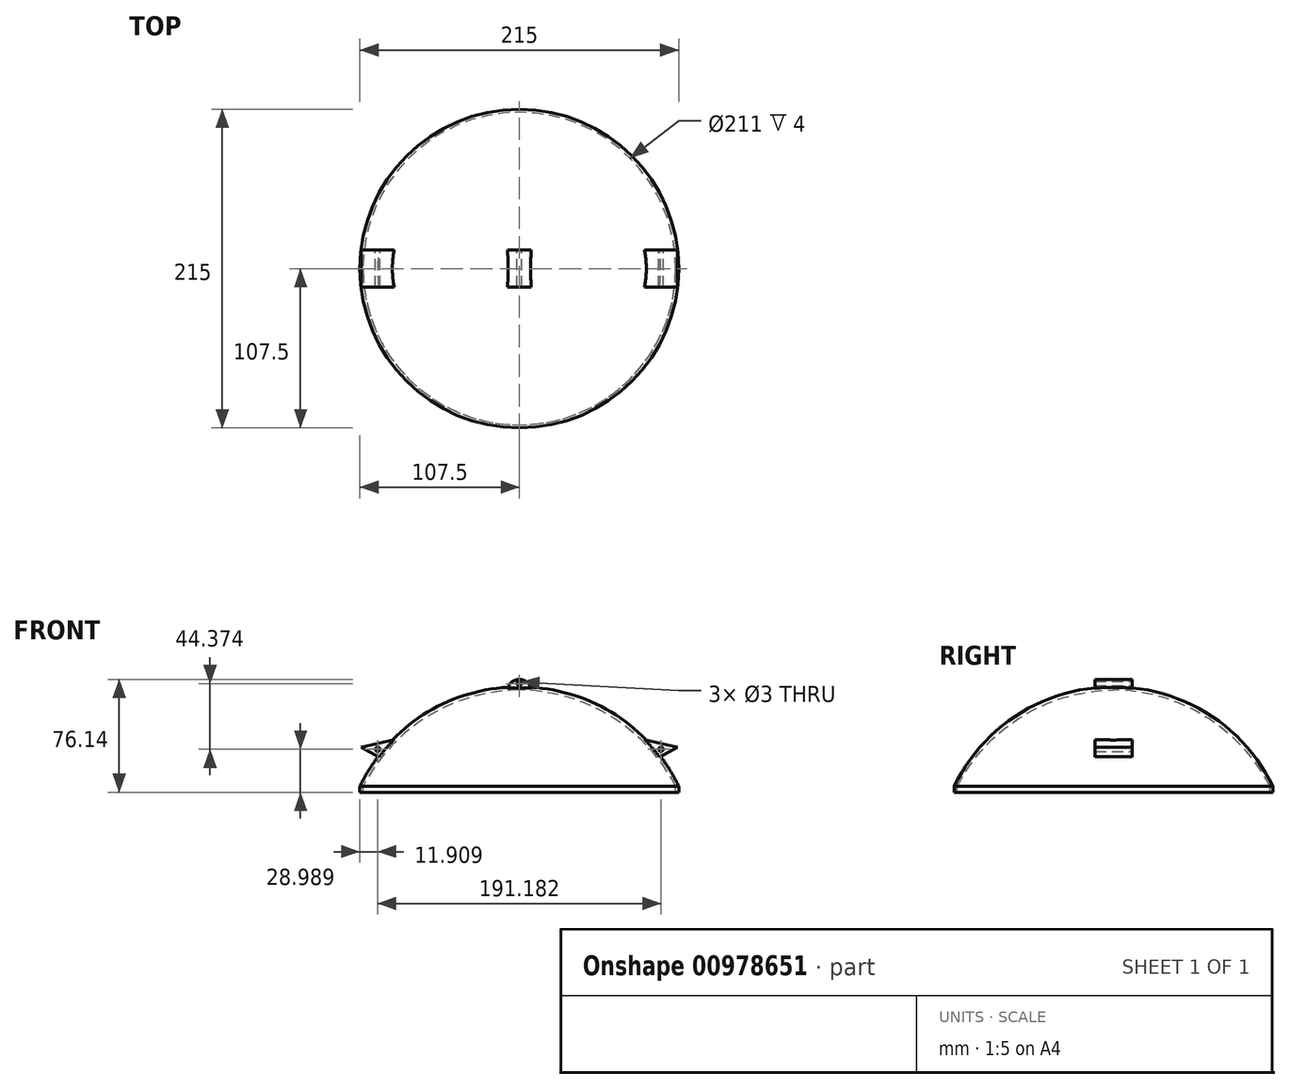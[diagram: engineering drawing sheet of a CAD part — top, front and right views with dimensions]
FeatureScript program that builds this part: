
annotation { "Feature Type Name" : "Feature", "Feature Type Description" : "" }
export const myFeature = defineFeature(function(context is Context, id is Id, definition is map)
    precondition{}
    {
        {
            var Q0;
            Q0=qCreatedBy(makeId("Front.planeOp"),FACE);
            var sketch = newSketch(context, id + "F0", { "sketchPlane" : qUnion([Q0])});
            skLineSegment(sketch, "E0", {"start": v(0, 0) * mm, "end": v(-107.5, 0) * mm});
            skLineSegment(sketch, "E1", {"start": v(0, 0) * mm, "end": v(0, 67) * mm});
            skArc(sketch, "E2", {"start": v(0, 67) * mm, "mid": v(-63.47, 49.1) * mm, "end": v(-107.5, 0) * mm});
            skSolve(sketch);
        }
        {
            var Q0;
            Q0=qCreatedBy(makeId("Front.planeOp"),FACE);
            var sketch = newSketch(context, id + "F1", { "sketchPlane" : qUnion([Q0])});
            skLineSegment(sketch, "E3", {"start": v(0, 0) * mm, "end": v(-105.5, 0) * mm});
            skLineSegment(sketch, "E4", {"start": v(0, 0) * mm, "end": v(0, 65) * mm});
            skArc(sketch, "E5", {"start": v(0, 65) * mm, "mid": v(-61.79, 47.17) * mm, "end": v(-105.5, 0) * mm});
            skSolve(sketch);
        }
        {
            var Q0;
            Q0=qSketchRegion(id+"F0",true);
            var Q1;
            Q1=sQuery(id+"F0.wireOp",EDGE,"E1");
            revolve(context, id + "F2", {"surfaceOperationType" : NewSurfaceOperationType.NEW, "entities" : qUnion([Q0]), "axis" : qUnion([Q1]), "revolveType" : RevolveType.FULL});
        }
        {
            var Q0;
            Q0=qSketchRegion(id+"F1",true);
            var Q1;
            Q1=sQuery(id+"F1.wireOp",EDGE,"E4");
            revolve(context, id + "F3", {"operationType" : NewBodyOperationType.REMOVE, "surfaceOperationType" : NewSurfaceOperationType.NEW, "entities" : qUnion([Q0]), "axis" : qUnion([Q1]), "revolveType" : RevolveType.FULL, "oppositeDirection" : true});
        }
        {
            var Q0;
            Q0=qCreatedBy(makeId("Front.planeOp"),FACE);
            var sketch = newSketch(context, id + "F4", { "sketchPlane" : qUnion([Q0])});
            skLineSegment(sketch, "E6.bottom", {"start": v(-105.5, 0) * mm, "end": v(-107.5, 0) * mm});
            skLineSegment(sketch, "E6.top", {"start": v(-105.5, -4) * mm, "end": v(-107.5, -4) * mm});
            skLineSegment(sketch, "E6.left", {"start": v(-105.5, 0) * mm, "end": v(-105.5, -4) * mm});
            skLineSegment(sketch, "E6.right", {"start": v(-107.5, 0) * mm, "end": v(-107.5, -4) * mm});
            skLineSegment(sketch, "E7", {"start": v(0, 0) * mm, "end": v(0, -6.13) * mm});
            skSolve(sketch);
        }
        {
            var Q0;
            Q0=qSketchRegion(id+"F4",true);
            var Q1;
            Q1=sQuery(id+"F4.wireOp",EDGE,"E7");
            revolve(context, id + "F5", {"operationType" : NewBodyOperationType.ADD, "surfaceOperationType" : NewSurfaceOperationType.NEW, "entities" : qUnion([Q0]), "axis" : qUnion([Q1]), "revolveType" : RevolveType.FULL});
        }
        {
            var Q0;
            Q0=qCreatedBy(makeId("Front.planeOp"),FACE);
            var sketch = newSketch(context, id + "F6", { "sketchPlane" : qUnion([Q0])});
            skLineSegment(sketch, "E8", {"start": v(-93.44, 19.13) * mm, "end": v(-84.53, 31.51) * mm});
            skCircle(sketch, "E9", {"center": v(-95.6, 24.99) * mm, "radius": 1.5 * mm});
            skLineSegment(sketch, "E10", {"start": v(-93.44, 19.13) * mm, "end": v(-106.58, 26.37) * mm});
            skLineSegment(sketch, "E11", {"start": v(-106.58, 26.37) * mm, "end": v(-84.53, 31.51) * mm});
            skSolve(sketch);
        }
        {
            var Q0;
            Q0=qSketchRegion(id+"F6",true);
            extrude(context, id + "F7", {"entities" : qUnion([Q0]), "operationType" : NewBodyOperationType.ADD, "endBound" : BoundingType.SYMMETRIC, "depth" : 25 * mm, "offsetDistance" : 25 * mm});
        }
        {
            var Q0;
            Q0=qCreatedBy(makeId("Front.planeOp"),FACE);
            var sketch = newSketch(context, id + "F8", { "sketchPlane" : qUnion([Q0])});
            skLineSegment(sketch, "E12.MirrorCS", {"start": v(93.44, 19.13) * mm, "end": v(106.58, 26.37) * mm});
            skLineSegment(sketch, "E13.MirrorCS", {"start": v(106.58, 26.37) * mm, "end": v(84.53, 31.51) * mm});
            skLineSegment(sketch, "E14.MirrorCS", {"start": v(93.44, 19.13) * mm, "end": v(84.53, 31.51) * mm});
            skCircle(sketch, "E15.MirrorC", {"center": v(95.6, 24.99) * mm, "radius": 1.5 * mm});
            skSolve(sketch);
        }
        {
            var Q0;
            Q0=qSketchRegion(id+"F8",true);
            extrude(context, id + "F9", {"entities" : qUnion([Q0]), "operationType" : NewBodyOperationType.ADD, "endBound" : BoundingType.SYMMETRIC, "depth" : 25 * mm, "offsetDistance" : 25 * mm});
        }
        {
            var Q0;
            Q0=qCreatedBy(makeId("Front.planeOp"),FACE);
            var sketch = newSketch(context, id + "F10", { "sketchPlane" : qUnion([Q0])});
            skLineSegment(sketch, "E16", {"start": v(-8, 65.74) * mm, "end": v(8, 65.74) * mm});
            skArc(sketch, "E17", {"start": v(8, 65.74) * mm, "mid": v(0, 72.14) * mm, "end": v(-8, 65.74) * mm});
            skCircle(sketch, "E18", {"center": v(0, 69.36) * mm, "radius": 1.5 * mm});
            skSolve(sketch);
        }
        {
            var Q0;
            Q0=qSketchRegion(id+"F10",true);
            extrude(context, id + "F11", {"entities" : qUnion([Q0]), "operationType" : NewBodyOperationType.ADD, "endBound" : BoundingType.SYMMETRIC, "depth" : 25 * mm, "offsetDistance" : 25 * mm});
        }
        {
            var Q0;
            Q0=qCreatedBy(makeId("Front.planeOp"),FACE);
            cPlane(context, id + "F12", {"entities" : qUnion([Q0]), "cplaneType" : CPlaneType.OFFSET, "offset" : 60 * mm, "width" : 150 * mm, "height" : 150 * mm});
        }
    });
